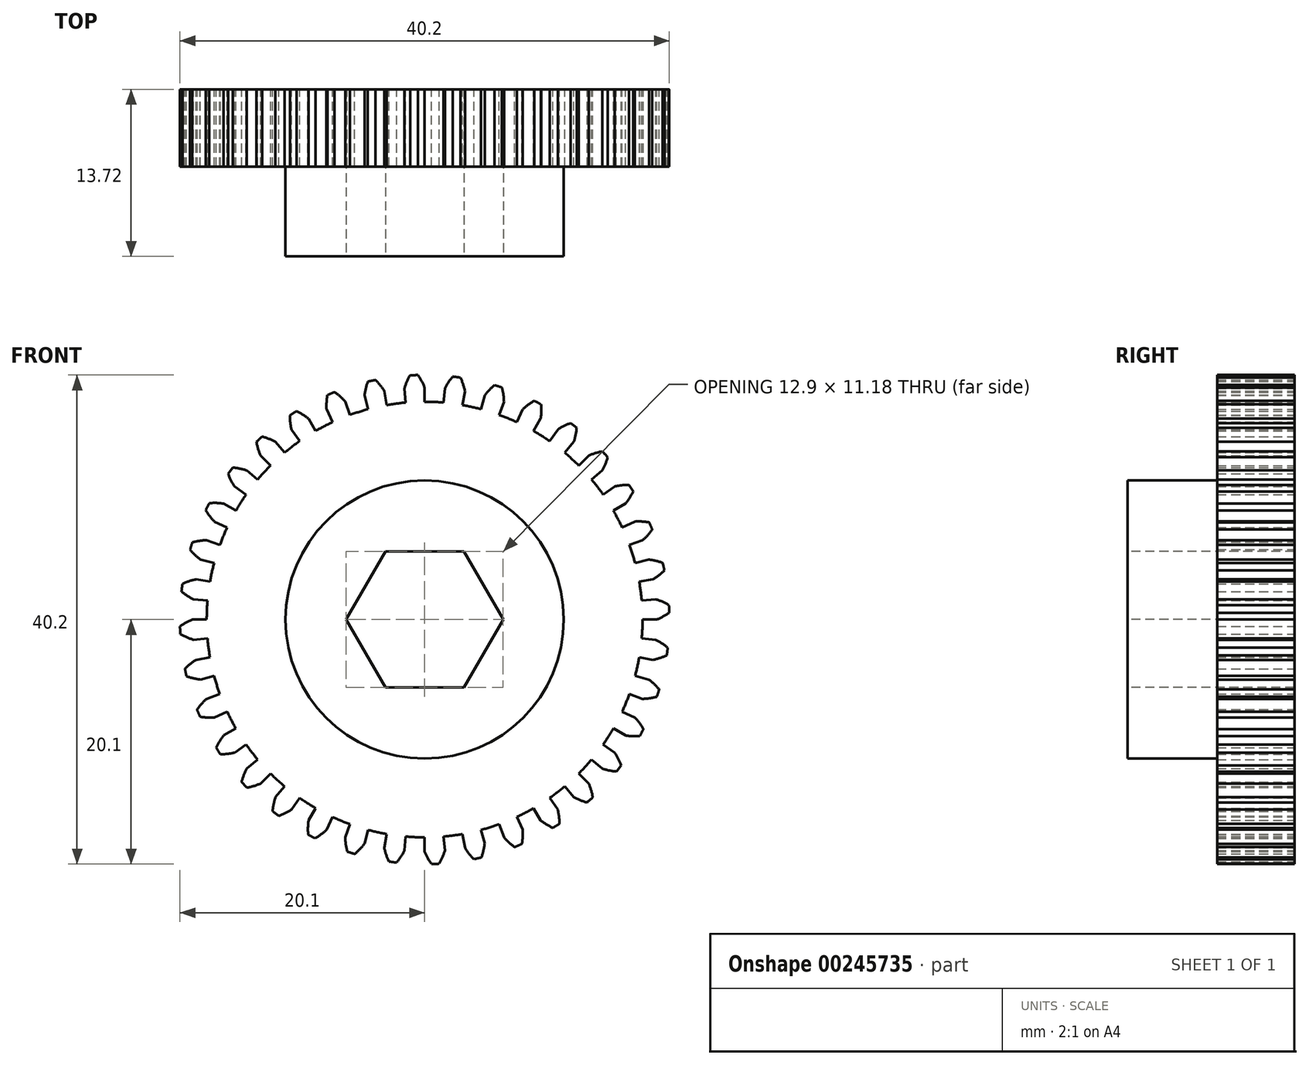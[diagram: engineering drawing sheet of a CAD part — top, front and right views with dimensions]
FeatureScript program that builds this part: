
annotation { "Feature Type Name" : "Feature", "Feature Type Description" : "" }
export const myFeature = defineFeature(function(context is Context, id is Id, definition is map)
    precondition{}
    {
        {
            var Q0;
            Q0=qCreatedBy(makeId("Front.planeOp"),FACE);
            var sketch = newSketch(context, id + "F0", { "sketchPlane" : qUnion([Q0])});
            skArc(sketch, "E0", {"start": v(0, 19.05) * mm, "mid": v(0, 19.05) * mm, "end": v(0, 19.05) * mm});
            skArc(sketch, "E1", {"start": v(-0.56, 20.1) * mm, "mid": v(-0.72, 20.1) * mm, "end": v(-0.88, 20.08) * mm});
            skLineSegment(sketch, "E2", {"start": v(0, 17.9) * mm, "end": v(0, 19.06) * mm});
            skLineSegment(sketch, "E3", {"start": v(0, 0) * mm, "end": v(-1.82, 41.68) * mm, "construction": true});
            skArc(sketch, "E4", {"start": v(1.56, 17.83) * mm, "mid": v(0.78, 17.88) * mm, "end": v(0, 17.9) * mm});
            skPoint(sketch, "E5", {"position": v(-4.44, 17.33) * mm});
            skArc(sketch, "E6.trimOffspring", {"start": v(0, 19.05) * mm, "mid": v(-0.25, 19.6) * mm, "end": v(-0.56, 20.1) * mm});
            skArc(sketch, "E7.MirrorCS", {"start": v(-1.66, 18.98) * mm, "mid": v(-1.46, 19.54) * mm, "end": v(-1.2, 20.07) * mm});
            skArc(sketch, "E8.MirrorCS", {"start": v(-1.2, 20.07) * mm, "mid": v(-1.04, 20.08) * mm, "end": v(-0.88, 20.08) * mm});
            skLineSegment(sketch, "E9.MirrorCS", {"start": v(-1.56, 17.83) * mm, "end": v(-1.66, 18.99) * mm});
            skPoint(sketch, "E10.orphan", {"position": v(-3.59, 41.01) * mm});
            skPoint(sketch, "E11.orphan", {"position": v(0, 41.17) * mm});
            skLineSegment(sketch, "E12.1.0", {"start": v(-4.63, 17.3) * mm, "end": v(-4.93, 18.4) * mm});
            skArc(sketch, "E12.1.1", {"start": v(-4.93, 18.4) * mm, "mid": v(-4.83, 18.99) * mm, "end": v(-4.66, 19.56) * mm});
            skArc(sketch, "E12.1.2", {"start": v(-4.66, 19.56) * mm, "mid": v(-4.5, 19.6) * mm, "end": v(-4.35, 19.63) * mm});
            skArc(sketch, "E12.1.3", {"start": v(-4.04, 19.7) * mm, "mid": v(-4.2, 19.66) * mm, "end": v(-4.35, 19.63) * mm});
            skArc(sketch, "E12.1.4", {"start": v(-3.3, 18.76) * mm, "mid": v(-3.64, 19.25) * mm, "end": v(-4.04, 19.7) * mm});
            skLineSegment(sketch, "E12.1.5", {"start": v(-3.1, 17.63) * mm, "end": v(-3.3, 18.77) * mm});
            skLineSegment(sketch, "E12.2.0", {"start": v(-7.57, 16.22) * mm, "end": v(-8.05, 17.27) * mm});
            skArc(sketch, "E12.2.1", {"start": v(-8.05, 17.26) * mm, "mid": v(-8.06, 17.86) * mm, "end": v(-7.99, 18.45) * mm});
            skArc(sketch, "E12.2.2", {"start": v(-7.99, 18.45) * mm, "mid": v(-7.84, 18.51) * mm, "end": v(-7.7, 18.57) * mm});
            skArc(sketch, "E12.2.3", {"start": v(-7.4, 18.7) * mm, "mid": v(-7.55, 18.63) * mm, "end": v(-7.7, 18.57) * mm});
            skArc(sketch, "E12.2.4", {"start": v(-6.51, 17.9) * mm, "mid": v(-6.93, 18.33) * mm, "end": v(-7.4, 18.7) * mm});
            skLineSegment(sketch, "E12.2.5", {"start": v(-6.12, 16.82) * mm, "end": v(-6.52, 17.9) * mm});
            skLineSegment(sketch, "E12.3.0", {"start": v(-10.27, 14.66) * mm, "end": v(-10.93, 15.61) * mm});
            skArc(sketch, "E12.3.1", {"start": v(-10.93, 15.6) * mm, "mid": v(-11.04, 16.19) * mm, "end": v(-11.07, 16.78) * mm});
            skArc(sketch, "E12.3.2", {"start": v(-11.07, 16.78) * mm, "mid": v(-10.94, 16.87) * mm, "end": v(-10.8, 16.96) * mm});
            skArc(sketch, "E12.3.3", {"start": v(-10.53, 17.12) * mm, "mid": v(-10.67, 17.04) * mm, "end": v(-10.8, 16.96) * mm});
            skArc(sketch, "E12.3.4", {"start": v(-9.52, 16.5) * mm, "mid": v(-10, 16.84) * mm, "end": v(-10.53, 17.12) * mm});
            skLineSegment(sketch, "E12.3.5", {"start": v(-8.95, 15.5) * mm, "end": v(-9.53, 16.5) * mm});
            skLineSegment(sketch, "E12.4.0", {"start": v(-12.66, 12.66) * mm, "end": v(-13.48, 13.48) * mm});
            skArc(sketch, "E12.4.1", {"start": v(-13.47, 13.47) * mm, "mid": v(-13.68, 14.03) * mm, "end": v(-13.81, 14.6) * mm});
            skArc(sketch, "E12.4.2", {"start": v(-13.81, 14.6) * mm, "mid": v(-13.7, 14.71) * mm, "end": v(-13.58, 14.82) * mm});
            skArc(sketch, "E12.4.3", {"start": v(-13.35, 15.04) * mm, "mid": v(-13.46, 14.93) * mm, "end": v(-13.58, 14.82) * mm});
            skArc(sketch, "E12.4.4", {"start": v(-12.24, 14.6) * mm, "mid": v(-12.78, 14.85) * mm, "end": v(-13.35, 15.04) * mm});
            skLineSegment(sketch, "E12.4.5", {"start": v(-11.5, 13.71) * mm, "end": v(-12.25, 14.6) * mm});
            skLineSegment(sketch, "E12.5.0", {"start": v(-14.66, 10.27) * mm, "end": v(-15.61, 10.93) * mm});
            skArc(sketch, "E12.5.1", {"start": v(-15.6, 10.92) * mm, "mid": v(-15.9, 11.44) * mm, "end": v(-16.14, 11.99) * mm});
            skArc(sketch, "E12.5.2", {"start": v(-16.14, 11.99) * mm, "mid": v(-16.05, 12.11) * mm, "end": v(-15.95, 12.24) * mm});
            skArc(sketch, "E12.5.3", {"start": v(-15.75, 12.49) * mm, "mid": v(-15.85, 12.36) * mm, "end": v(-15.95, 12.24) * mm});
            skArc(sketch, "E12.5.4", {"start": v(-14.6, 12.25) * mm, "mid": v(-15.17, 12.4) * mm, "end": v(-15.75, 12.49) * mm});
            skLineSegment(sketch, "E12.5.5", {"start": v(-13.71, 11.5) * mm, "end": v(-14.6, 12.25) * mm});
            skLineSegment(sketch, "E12.6.0", {"start": v(-16.22, 7.57) * mm, "end": v(-17.27, 8.05) * mm});
            skArc(sketch, "E12.6.1", {"start": v(-17.27, 8.05) * mm, "mid": v(-17.65, 8.5) * mm, "end": v(-17.98, 9) * mm});
            skArc(sketch, "E12.6.2", {"start": v(-17.98, 9) * mm, "mid": v(-17.9, 9.14) * mm, "end": v(-17.83, 9.28) * mm});
            skArc(sketch, "E12.6.3", {"start": v(-17.68, 9.56) * mm, "mid": v(-17.76, 9.42) * mm, "end": v(-17.83, 9.28) * mm});
            skArc(sketch, "E12.6.4", {"start": v(-16.5, 9.53) * mm, "mid": v(-17.09, 9.58) * mm, "end": v(-17.68, 9.56) * mm});
            skLineSegment(sketch, "E12.6.5", {"start": v(-15.5, 8.95) * mm, "end": v(-16.5, 9.53) * mm});
            skLineSegment(sketch, "E12.7.0", {"start": v(-17.3, 4.63) * mm, "end": v(-18.4, 4.93) * mm});
            skArc(sketch, "E12.7.1", {"start": v(-18.4, 4.93) * mm, "mid": v(-18.86, 5.3) * mm, "end": v(-19.27, 5.74) * mm});
            skArc(sketch, "E12.7.2", {"start": v(-19.27, 5.74) * mm, "mid": v(-19.22, 5.9) * mm, "end": v(-19.17, 6.05) * mm});
            skArc(sketch, "E12.7.3", {"start": v(-19.08, 6.35) * mm, "mid": v(-19.13, 6.2) * mm, "end": v(-19.17, 6.05) * mm});
            skArc(sketch, "E12.7.4", {"start": v(-17.9, 6.52) * mm, "mid": v(-18.5, 6.47) * mm, "end": v(-19.08, 6.35) * mm});
            skLineSegment(sketch, "E12.7.5", {"start": v(-16.82, 6.12) * mm, "end": v(-17.9, 6.52) * mm});
            skLineSegment(sketch, "E12.8.0", {"start": v(-17.83, 1.56) * mm, "end": v(-18.99, 1.66) * mm});
            skArc(sketch, "E12.8.1", {"start": v(-18.98, 1.66) * mm, "mid": v(-19.5, 1.95) * mm, "end": v(-19.97, 2.3) * mm});
            skArc(sketch, "E12.8.2", {"start": v(-19.97, 2.3) * mm, "mid": v(-19.95, 2.47) * mm, "end": v(-19.93, 2.62) * mm});
            skArc(sketch, "E12.8.3", {"start": v(-19.89, 2.94) * mm, "mid": v(-19.91, 2.78) * mm, "end": v(-19.93, 2.62) * mm});
            skArc(sketch, "E12.8.4", {"start": v(-18.76, 3.31) * mm, "mid": v(-19.34, 3.16) * mm, "end": v(-19.89, 2.94) * mm});
            skLineSegment(sketch, "E12.8.5", {"start": v(-17.63, 3.1) * mm, "end": v(-18.77, 3.3) * mm});
            skLineSegment(sketch, "E12.9.0", {"start": v(-17.83, -1.56) * mm, "end": v(-18.99, -1.66) * mm});
            skArc(sketch, "E12.9.1", {"start": v(-18.98, -1.66) * mm, "mid": v(-19.54, -1.46) * mm, "end": v(-20.07, -1.2) * mm});
            skArc(sketch, "E12.9.2", {"start": v(-20.07, -1.2) * mm, "mid": v(-20.08, -1.04) * mm, "end": v(-20.08, -0.88) * mm});
            skArc(sketch, "E12.9.3", {"start": v(-20.1, -0.56) * mm, "mid": v(-20.1, -0.72) * mm, "end": v(-20.08, -0.88) * mm});
            skArc(sketch, "E12.9.4", {"start": v(-19.05, 0) * mm, "mid": v(-19.6, -0.25) * mm, "end": v(-20.1, -0.56) * mm});
            skLineSegment(sketch, "E12.9.5", {"start": v(-17.9, 0) * mm, "end": v(-19.06, 0) * mm});
            skLineSegment(sketch, "E12.10.0", {"start": v(-17.3, -4.63) * mm, "end": v(-18.4, -4.93) * mm});
            skArc(sketch, "E12.10.1", {"start": v(-18.4, -4.93) * mm, "mid": v(-18.99, -4.83) * mm, "end": v(-19.56, -4.66) * mm});
            skArc(sketch, "E12.10.2", {"start": v(-19.56, -4.66) * mm, "mid": v(-19.6, -4.5) * mm, "end": v(-19.63, -4.35) * mm});
            skArc(sketch, "E12.10.3", {"start": v(-19.7, -4.04) * mm, "mid": v(-19.66, -4.2) * mm, "end": v(-19.63, -4.35) * mm});
            skArc(sketch, "E12.10.4", {"start": v(-18.76, -3.3) * mm, "mid": v(-19.25, -3.64) * mm, "end": v(-19.7, -4.04) * mm});
            skLineSegment(sketch, "E12.10.5", {"start": v(-17.63, -3.1) * mm, "end": v(-18.77, -3.3) * mm});
            skLineSegment(sketch, "E12.11.0", {"start": v(-16.22, -7.57) * mm, "end": v(-17.27, -8.05) * mm});
            skArc(sketch, "E12.11.1", {"start": v(-17.26, -8.05) * mm, "mid": v(-17.86, -8.06) * mm, "end": v(-18.45, -7.99) * mm});
            skArc(sketch, "E12.11.2", {"start": v(-18.45, -7.99) * mm, "mid": v(-18.51, -7.84) * mm, "end": v(-18.57, -7.7) * mm});
            skArc(sketch, "E12.11.3", {"start": v(-18.7, -7.4) * mm, "mid": v(-18.63, -7.55) * mm, "end": v(-18.57, -7.7) * mm});
            skArc(sketch, "E12.11.4", {"start": v(-17.9, -6.51) * mm, "mid": v(-18.33, -6.93) * mm, "end": v(-18.7, -7.4) * mm});
            skLineSegment(sketch, "E12.11.5", {"start": v(-16.82, -6.12) * mm, "end": v(-17.9, -6.52) * mm});
            skLineSegment(sketch, "E12.12.0", {"start": v(-14.66, -10.27) * mm, "end": v(-15.61, -10.93) * mm});
            skArc(sketch, "E12.12.1", {"start": v(-15.6, -10.93) * mm, "mid": v(-16.19, -11.04) * mm, "end": v(-16.78, -11.07) * mm});
            skArc(sketch, "E12.12.2", {"start": v(-16.78, -11.07) * mm, "mid": v(-16.87, -10.94) * mm, "end": v(-16.96, -10.8) * mm});
            skArc(sketch, "E12.12.3", {"start": v(-17.12, -10.53) * mm, "mid": v(-17.04, -10.67) * mm, "end": v(-16.96, -10.8) * mm});
            skArc(sketch, "E12.12.4", {"start": v(-16.5, -9.52) * mm, "mid": v(-16.84, -10) * mm, "end": v(-17.12, -10.53) * mm});
            skLineSegment(sketch, "E12.12.5", {"start": v(-15.5, -8.95) * mm, "end": v(-16.5, -9.53) * mm});
            skLineSegment(sketch, "E12.13.0", {"start": v(-12.66, -12.66) * mm, "end": v(-13.48, -13.48) * mm});
            skArc(sketch, "E12.13.1", {"start": v(-13.47, -13.47) * mm, "mid": v(-14.03, -13.68) * mm, "end": v(-14.6, -13.81) * mm});
            skArc(sketch, "E12.13.2", {"start": v(-14.6, -13.81) * mm, "mid": v(-14.71, -13.7) * mm, "end": v(-14.82, -13.58) * mm});
            skArc(sketch, "E12.13.3", {"start": v(-15.04, -13.35) * mm, "mid": v(-14.93, -13.46) * mm, "end": v(-14.82, -13.58) * mm});
            skArc(sketch, "E12.13.4", {"start": v(-14.6, -12.24) * mm, "mid": v(-14.85, -12.78) * mm, "end": v(-15.04, -13.35) * mm});
            skLineSegment(sketch, "E12.13.5", {"start": v(-13.71, -11.5) * mm, "end": v(-14.6, -12.25) * mm});
            skLineSegment(sketch, "E12.14.0", {"start": v(-10.27, -14.66) * mm, "end": v(-10.93, -15.61) * mm});
            skArc(sketch, "E12.14.1", {"start": v(-10.92, -15.6) * mm, "mid": v(-11.44, -15.9) * mm, "end": v(-11.99, -16.14) * mm});
            skArc(sketch, "E12.14.2", {"start": v(-11.99, -16.14) * mm, "mid": v(-12.11, -16.05) * mm, "end": v(-12.24, -15.95) * mm});
            skArc(sketch, "E12.14.3", {"start": v(-12.49, -15.75) * mm, "mid": v(-12.36, -15.85) * mm, "end": v(-12.24, -15.95) * mm});
            skArc(sketch, "E12.14.4", {"start": v(-12.25, -14.6) * mm, "mid": v(-12.4, -15.17) * mm, "end": v(-12.49, -15.75) * mm});
            skLineSegment(sketch, "E12.14.5", {"start": v(-11.5, -13.71) * mm, "end": v(-12.25, -14.6) * mm});
            skLineSegment(sketch, "E12.15.0", {"start": v(-7.57, -16.22) * mm, "end": v(-8.05, -17.27) * mm});
            skArc(sketch, "E12.15.1", {"start": v(-8.05, -17.27) * mm, "mid": v(-8.5, -17.65) * mm, "end": v(-9, -17.98) * mm});
            skArc(sketch, "E12.15.2", {"start": v(-9, -17.98) * mm, "mid": v(-9.14, -17.9) * mm, "end": v(-9.28, -17.83) * mm});
            skArc(sketch, "E12.15.3", {"start": v(-9.56, -17.68) * mm, "mid": v(-9.42, -17.76) * mm, "end": v(-9.28, -17.83) * mm});
            skArc(sketch, "E12.15.4", {"start": v(-9.53, -16.5) * mm, "mid": v(-9.58, -17.09) * mm, "end": v(-9.56, -17.68) * mm});
            skLineSegment(sketch, "E12.15.5", {"start": v(-8.95, -15.5) * mm, "end": v(-9.53, -16.5) * mm});
            skLineSegment(sketch, "E12.16.0", {"start": v(-4.63, -17.3) * mm, "end": v(-4.93, -18.4) * mm});
            skArc(sketch, "E12.16.1", {"start": v(-4.93, -18.4) * mm, "mid": v(-5.3, -18.86) * mm, "end": v(-5.74, -19.27) * mm});
            skArc(sketch, "E12.16.2", {"start": v(-5.74, -19.27) * mm, "mid": v(-5.9, -19.22) * mm, "end": v(-6.05, -19.17) * mm});
            skArc(sketch, "E12.16.3", {"start": v(-6.35, -19.08) * mm, "mid": v(-6.2, -19.13) * mm, "end": v(-6.05, -19.17) * mm});
            skArc(sketch, "E12.16.4", {"start": v(-6.52, -17.9) * mm, "mid": v(-6.47, -18.5) * mm, "end": v(-6.35, -19.08) * mm});
            skLineSegment(sketch, "E12.16.5", {"start": v(-6.12, -16.82) * mm, "end": v(-6.52, -17.9) * mm});
            skLineSegment(sketch, "E12.17.0", {"start": v(-1.56, -17.83) * mm, "end": v(-1.66, -18.99) * mm});
            skArc(sketch, "E12.17.1", {"start": v(-1.66, -18.98) * mm, "mid": v(-1.95, -19.5) * mm, "end": v(-2.3, -19.97) * mm});
            skArc(sketch, "E12.17.2", {"start": v(-2.3, -19.97) * mm, "mid": v(-2.47, -19.95) * mm, "end": v(-2.62, -19.93) * mm});
            skArc(sketch, "E12.17.3", {"start": v(-2.94, -19.89) * mm, "mid": v(-2.78, -19.91) * mm, "end": v(-2.62, -19.93) * mm});
            skArc(sketch, "E12.17.4", {"start": v(-3.31, -18.76) * mm, "mid": v(-3.16, -19.34) * mm, "end": v(-2.94, -19.89) * mm});
            skLineSegment(sketch, "E12.17.5", {"start": v(-3.1, -17.63) * mm, "end": v(-3.3, -18.77) * mm});
            skLineSegment(sketch, "E12.18.0", {"start": v(1.56, -17.83) * mm, "end": v(1.66, -18.99) * mm});
            skArc(sketch, "E12.18.1", {"start": v(1.66, -18.98) * mm, "mid": v(1.46, -19.54) * mm, "end": v(1.2, -20.07) * mm});
            skArc(sketch, "E12.18.2", {"start": v(1.2, -20.07) * mm, "mid": v(1.04, -20.08) * mm, "end": v(0.88, -20.08) * mm});
            skArc(sketch, "E12.18.3", {"start": v(0.56, -20.1) * mm, "mid": v(0.72, -20.1) * mm, "end": v(0.88, -20.08) * mm});
            skArc(sketch, "E12.18.4", {"start": v(0, -19.05) * mm, "mid": v(0.25, -19.6) * mm, "end": v(0.56, -20.1) * mm});
            skLineSegment(sketch, "E12.18.5", {"start": v(0, -17.9) * mm, "end": v(0, -19.06) * mm});
            skLineSegment(sketch, "E12.19.0", {"start": v(4.63, -17.3) * mm, "end": v(4.93, -18.4) * mm});
            skArc(sketch, "E12.19.1", {"start": v(4.93, -18.4) * mm, "mid": v(4.83, -18.99) * mm, "end": v(4.66, -19.56) * mm});
            skArc(sketch, "E12.19.2", {"start": v(4.66, -19.56) * mm, "mid": v(4.5, -19.6) * mm, "end": v(4.35, -19.63) * mm});
            skArc(sketch, "E12.19.3", {"start": v(4.04, -19.7) * mm, "mid": v(4.2, -19.66) * mm, "end": v(4.35, -19.63) * mm});
            skArc(sketch, "E12.19.4", {"start": v(3.3, -18.76) * mm, "mid": v(3.64, -19.25) * mm, "end": v(4.04, -19.7) * mm});
            skLineSegment(sketch, "E12.19.5", {"start": v(3.1, -17.63) * mm, "end": v(3.3, -18.77) * mm});
            skLineSegment(sketch, "E12.20.0", {"start": v(7.57, -16.22) * mm, "end": v(8.05, -17.27) * mm});
            skArc(sketch, "E12.20.1", {"start": v(8.05, -17.26) * mm, "mid": v(8.06, -17.86) * mm, "end": v(7.99, -18.45) * mm});
            skArc(sketch, "E12.20.2", {"start": v(7.99, -18.45) * mm, "mid": v(7.84, -18.51) * mm, "end": v(7.7, -18.57) * mm});
            skArc(sketch, "E12.20.3", {"start": v(7.4, -18.7) * mm, "mid": v(7.55, -18.63) * mm, "end": v(7.7, -18.57) * mm});
            skArc(sketch, "E12.20.4", {"start": v(6.51, -17.9) * mm, "mid": v(6.93, -18.33) * mm, "end": v(7.4, -18.7) * mm});
            skLineSegment(sketch, "E12.20.5", {"start": v(6.12, -16.82) * mm, "end": v(6.52, -17.9) * mm});
            skLineSegment(sketch, "E12.21.0", {"start": v(10.27, -14.66) * mm, "end": v(10.93, -15.61) * mm});
            skArc(sketch, "E12.21.1", {"start": v(10.93, -15.6) * mm, "mid": v(11.04, -16.19) * mm, "end": v(11.07, -16.78) * mm});
            skArc(sketch, "E12.21.2", {"start": v(11.07, -16.78) * mm, "mid": v(10.94, -16.87) * mm, "end": v(10.8, -16.96) * mm});
            skArc(sketch, "E12.21.3", {"start": v(10.53, -17.12) * mm, "mid": v(10.67, -17.04) * mm, "end": v(10.8, -16.96) * mm});
            skArc(sketch, "E12.21.4", {"start": v(9.52, -16.5) * mm, "mid": v(10, -16.84) * mm, "end": v(10.53, -17.12) * mm});
            skLineSegment(sketch, "E12.21.5", {"start": v(8.95, -15.5) * mm, "end": v(9.53, -16.5) * mm});
            skLineSegment(sketch, "E12.22.0", {"start": v(12.66, -12.66) * mm, "end": v(13.48, -13.48) * mm});
            skArc(sketch, "E12.22.1", {"start": v(13.47, -13.47) * mm, "mid": v(13.68, -14.03) * mm, "end": v(13.81, -14.6) * mm});
            skArc(sketch, "E12.22.2", {"start": v(13.81, -14.6) * mm, "mid": v(13.7, -14.71) * mm, "end": v(13.58, -14.82) * mm});
            skArc(sketch, "E12.22.3", {"start": v(13.35, -15.04) * mm, "mid": v(13.46, -14.93) * mm, "end": v(13.58, -14.82) * mm});
            skArc(sketch, "E12.22.4", {"start": v(12.24, -14.6) * mm, "mid": v(12.78, -14.85) * mm, "end": v(13.35, -15.04) * mm});
            skLineSegment(sketch, "E12.22.5", {"start": v(11.5, -13.71) * mm, "end": v(12.25, -14.6) * mm});
            skLineSegment(sketch, "E12.23.0", {"start": v(14.66, -10.27) * mm, "end": v(15.61, -10.93) * mm});
            skArc(sketch, "E12.23.1", {"start": v(15.6, -10.92) * mm, "mid": v(15.9, -11.44) * mm, "end": v(16.14, -11.99) * mm});
            skArc(sketch, "E12.23.2", {"start": v(16.14, -11.99) * mm, "mid": v(16.05, -12.11) * mm, "end": v(15.95, -12.24) * mm});
            skArc(sketch, "E12.23.3", {"start": v(15.75, -12.49) * mm, "mid": v(15.85, -12.36) * mm, "end": v(15.95, -12.24) * mm});
            skArc(sketch, "E12.23.4", {"start": v(14.6, -12.25) * mm, "mid": v(15.17, -12.4) * mm, "end": v(15.75, -12.49) * mm});
            skLineSegment(sketch, "E12.23.5", {"start": v(13.71, -11.5) * mm, "end": v(14.6, -12.25) * mm});
            skLineSegment(sketch, "E12.24.0", {"start": v(16.22, -7.57) * mm, "end": v(17.27, -8.05) * mm});
            skArc(sketch, "E12.24.1", {"start": v(17.27, -8.05) * mm, "mid": v(17.65, -8.5) * mm, "end": v(17.98, -9) * mm});
            skArc(sketch, "E12.24.2", {"start": v(17.98, -9) * mm, "mid": v(17.9, -9.14) * mm, "end": v(17.83, -9.28) * mm});
            skArc(sketch, "E12.24.3", {"start": v(17.68, -9.56) * mm, "mid": v(17.76, -9.42) * mm, "end": v(17.83, -9.28) * mm});
            skArc(sketch, "E12.24.4", {"start": v(16.5, -9.53) * mm, "mid": v(17.09, -9.58) * mm, "end": v(17.68, -9.56) * mm});
            skLineSegment(sketch, "E12.24.5", {"start": v(15.5, -8.95) * mm, "end": v(16.5, -9.53) * mm});
            skLineSegment(sketch, "E12.25.0", {"start": v(17.3, -4.63) * mm, "end": v(18.4, -4.93) * mm});
            skArc(sketch, "E12.25.1", {"start": v(18.4, -4.93) * mm, "mid": v(18.86, -5.3) * mm, "end": v(19.27, -5.74) * mm});
            skArc(sketch, "E12.25.2", {"start": v(19.27, -5.74) * mm, "mid": v(19.22, -5.9) * mm, "end": v(19.17, -6.05) * mm});
            skArc(sketch, "E12.25.3", {"start": v(19.08, -6.35) * mm, "mid": v(19.13, -6.2) * mm, "end": v(19.17, -6.05) * mm});
            skArc(sketch, "E12.25.4", {"start": v(17.9, -6.52) * mm, "mid": v(18.5, -6.47) * mm, "end": v(19.08, -6.35) * mm});
            skLineSegment(sketch, "E12.25.5", {"start": v(16.82, -6.12) * mm, "end": v(17.9, -6.52) * mm});
            skLineSegment(sketch, "E12.26.0", {"start": v(17.83, -1.56) * mm, "end": v(18.99, -1.66) * mm});
            skArc(sketch, "E12.26.1", {"start": v(18.98, -1.66) * mm, "mid": v(19.5, -1.95) * mm, "end": v(19.97, -2.3) * mm});
            skArc(sketch, "E12.26.2", {"start": v(19.97, -2.3) * mm, "mid": v(19.95, -2.47) * mm, "end": v(19.93, -2.62) * mm});
            skArc(sketch, "E12.26.3", {"start": v(19.89, -2.94) * mm, "mid": v(19.91, -2.78) * mm, "end": v(19.93, -2.62) * mm});
            skArc(sketch, "E12.26.4", {"start": v(18.76, -3.31) * mm, "mid": v(19.34, -3.16) * mm, "end": v(19.89, -2.94) * mm});
            skLineSegment(sketch, "E12.26.5", {"start": v(17.63, -3.1) * mm, "end": v(18.77, -3.3) * mm});
            skLineSegment(sketch, "E12.27.0", {"start": v(17.83, 1.56) * mm, "end": v(18.99, 1.66) * mm});
            skArc(sketch, "E12.27.1", {"start": v(18.98, 1.66) * mm, "mid": v(19.54, 1.46) * mm, "end": v(20.07, 1.2) * mm});
            skArc(sketch, "E12.27.2", {"start": v(20.07, 1.2) * mm, "mid": v(20.08, 1.04) * mm, "end": v(20.08, 0.88) * mm});
            skArc(sketch, "E12.27.3", {"start": v(20.1, 0.56) * mm, "mid": v(20.1, 0.72) * mm, "end": v(20.08, 0.88) * mm});
            skArc(sketch, "E12.27.4", {"start": v(19.05, 0) * mm, "mid": v(19.6, 0.25) * mm, "end": v(20.1, 0.56) * mm});
            skLineSegment(sketch, "E12.27.5", {"start": v(17.9, 0) * mm, "end": v(19.06, 0) * mm});
            skLineSegment(sketch, "E12.28.0", {"start": v(17.3, 4.63) * mm, "end": v(18.4, 4.93) * mm});
            skArc(sketch, "E12.28.1", {"start": v(18.4, 4.93) * mm, "mid": v(18.99, 4.83) * mm, "end": v(19.56, 4.66) * mm});
            skArc(sketch, "E12.28.2", {"start": v(19.56, 4.66) * mm, "mid": v(19.6, 4.5) * mm, "end": v(19.63, 4.35) * mm});
            skArc(sketch, "E12.28.3", {"start": v(19.7, 4.04) * mm, "mid": v(19.66, 4.2) * mm, "end": v(19.63, 4.35) * mm});
            skArc(sketch, "E12.28.4", {"start": v(18.76, 3.3) * mm, "mid": v(19.25, 3.64) * mm, "end": v(19.7, 4.04) * mm});
            skLineSegment(sketch, "E12.28.5", {"start": v(17.63, 3.1) * mm, "end": v(18.77, 3.3) * mm});
            skLineSegment(sketch, "E12.29.0", {"start": v(16.22, 7.57) * mm, "end": v(17.27, 8.05) * mm});
            skArc(sketch, "E12.29.1", {"start": v(17.26, 8.05) * mm, "mid": v(17.86, 8.06) * mm, "end": v(18.45, 7.99) * mm});
            skArc(sketch, "E12.29.2", {"start": v(18.45, 7.99) * mm, "mid": v(18.51, 7.84) * mm, "end": v(18.57, 7.7) * mm});
            skArc(sketch, "E12.29.3", {"start": v(18.7, 7.4) * mm, "mid": v(18.63, 7.55) * mm, "end": v(18.57, 7.7) * mm});
            skArc(sketch, "E12.29.4", {"start": v(17.9, 6.51) * mm, "mid": v(18.33, 6.93) * mm, "end": v(18.7, 7.4) * mm});
            skLineSegment(sketch, "E12.29.5", {"start": v(16.82, 6.12) * mm, "end": v(17.9, 6.52) * mm});
            skLineSegment(sketch, "E12.30.0", {"start": v(14.66, 10.27) * mm, "end": v(15.61, 10.93) * mm});
            skArc(sketch, "E12.30.1", {"start": v(15.6, 10.93) * mm, "mid": v(16.19, 11.04) * mm, "end": v(16.78, 11.07) * mm});
            skArc(sketch, "E12.30.2", {"start": v(16.78, 11.07) * mm, "mid": v(16.87, 10.94) * mm, "end": v(16.96, 10.8) * mm});
            skArc(sketch, "E12.30.3", {"start": v(17.12, 10.53) * mm, "mid": v(17.04, 10.67) * mm, "end": v(16.96, 10.8) * mm});
            skArc(sketch, "E12.30.4", {"start": v(16.5, 9.52) * mm, "mid": v(16.84, 10) * mm, "end": v(17.12, 10.53) * mm});
            skLineSegment(sketch, "E12.30.5", {"start": v(15.5, 8.95) * mm, "end": v(16.5, 9.53) * mm});
            skLineSegment(sketch, "E12.31.0", {"start": v(12.66, 12.66) * mm, "end": v(13.48, 13.48) * mm});
            skArc(sketch, "E12.31.1", {"start": v(13.47, 13.47) * mm, "mid": v(14.03, 13.68) * mm, "end": v(14.6, 13.81) * mm});
            skArc(sketch, "E12.31.2", {"start": v(14.6, 13.81) * mm, "mid": v(14.71, 13.7) * mm, "end": v(14.82, 13.58) * mm});
            skArc(sketch, "E12.31.3", {"start": v(15.04, 13.35) * mm, "mid": v(14.93, 13.46) * mm, "end": v(14.82, 13.58) * mm});
            skArc(sketch, "E12.31.4", {"start": v(14.6, 12.24) * mm, "mid": v(14.85, 12.78) * mm, "end": v(15.04, 13.35) * mm});
            skLineSegment(sketch, "E12.31.5", {"start": v(13.71, 11.5) * mm, "end": v(14.6, 12.25) * mm});
            skLineSegment(sketch, "E12.32.0", {"start": v(10.27, 14.66) * mm, "end": v(10.93, 15.61) * mm});
            skArc(sketch, "E12.32.1", {"start": v(10.92, 15.6) * mm, "mid": v(11.44, 15.9) * mm, "end": v(11.99, 16.14) * mm});
            skArc(sketch, "E12.32.2", {"start": v(11.99, 16.14) * mm, "mid": v(12.11, 16.05) * mm, "end": v(12.24, 15.95) * mm});
            skArc(sketch, "E12.32.3", {"start": v(12.49, 15.75) * mm, "mid": v(12.36, 15.85) * mm, "end": v(12.24, 15.95) * mm});
            skArc(sketch, "E12.32.4", {"start": v(12.25, 14.6) * mm, "mid": v(12.4, 15.17) * mm, "end": v(12.49, 15.75) * mm});
            skLineSegment(sketch, "E12.32.5", {"start": v(11.5, 13.71) * mm, "end": v(12.25, 14.6) * mm});
            skLineSegment(sketch, "E12.33.0", {"start": v(7.57, 16.22) * mm, "end": v(8.05, 17.27) * mm});
            skArc(sketch, "E12.33.1", {"start": v(8.05, 17.27) * mm, "mid": v(8.5, 17.65) * mm, "end": v(9, 17.98) * mm});
            skArc(sketch, "E12.33.2", {"start": v(9, 17.98) * mm, "mid": v(9.14, 17.9) * mm, "end": v(9.28, 17.83) * mm});
            skArc(sketch, "E12.33.3", {"start": v(9.56, 17.68) * mm, "mid": v(9.42, 17.76) * mm, "end": v(9.28, 17.83) * mm});
            skArc(sketch, "E12.33.4", {"start": v(9.53, 16.5) * mm, "mid": v(9.58, 17.09) * mm, "end": v(9.56, 17.68) * mm});
            skLineSegment(sketch, "E12.33.5", {"start": v(8.95, 15.5) * mm, "end": v(9.53, 16.5) * mm});
            skLineSegment(sketch, "E12.34.0", {"start": v(4.63, 17.3) * mm, "end": v(4.93, 18.4) * mm});
            skArc(sketch, "E12.34.1", {"start": v(4.93, 18.4) * mm, "mid": v(5.3, 18.86) * mm, "end": v(5.74, 19.27) * mm});
            skArc(sketch, "E12.34.2", {"start": v(5.74, 19.27) * mm, "mid": v(5.9, 19.22) * mm, "end": v(6.05, 19.17) * mm});
            skArc(sketch, "E12.34.3", {"start": v(6.35, 19.08) * mm, "mid": v(6.2, 19.13) * mm, "end": v(6.05, 19.17) * mm});
            skArc(sketch, "E12.34.4", {"start": v(6.52, 17.9) * mm, "mid": v(6.47, 18.5) * mm, "end": v(6.35, 19.08) * mm});
            skLineSegment(sketch, "E12.34.5", {"start": v(6.12, 16.82) * mm, "end": v(6.52, 17.9) * mm});
            skLineSegment(sketch, "E12.35.0", {"start": v(1.56, 17.83) * mm, "end": v(1.66, 18.99) * mm});
            skArc(sketch, "E12.35.1", {"start": v(1.66, 18.98) * mm, "mid": v(1.95, 19.5) * mm, "end": v(2.3, 19.97) * mm});
            skArc(sketch, "E12.35.2", {"start": v(2.3, 19.97) * mm, "mid": v(2.47, 19.95) * mm, "end": v(2.62, 19.93) * mm});
            skArc(sketch, "E12.35.3", {"start": v(2.94, 19.89) * mm, "mid": v(2.78, 19.91) * mm, "end": v(2.62, 19.93) * mm});
            skArc(sketch, "E12.35.4", {"start": v(3.31, 18.76) * mm, "mid": v(3.16, 19.34) * mm, "end": v(2.94, 19.89) * mm});
            skLineSegment(sketch, "E12.35.5", {"start": v(3.1, 17.63) * mm, "end": v(3.3, 18.77) * mm});
            skArc(sketch, "E13.trimOffspring", {"start": v(4.63, 17.3) * mm, "mid": v(3.87, 17.48) * mm, "end": v(3.1, 17.63) * mm});
            skArc(sketch, "E14.trimOffspring", {"start": v(7.57, 16.22) * mm, "mid": v(6.85, 16.54) * mm, "end": v(6.12, 16.82) * mm});
            skArc(sketch, "E15.trimOffspring", {"start": v(10.27, 14.66) * mm, "mid": v(9.62, 15.1) * mm, "end": v(8.95, 15.5) * mm});
            skArc(sketch, "E16.trimOffspring", {"start": v(12.66, 12.66) * mm, "mid": v(12.1, 13.2) * mm, "end": v(11.5, 13.71) * mm});
            skArc(sketch, "E17.trimOffspring", {"start": v(14.66, 10.27) * mm, "mid": v(14.2, 10.9) * mm, "end": v(13.71, 11.5) * mm});
            skArc(sketch, "E18.trimOffspring", {"start": v(16.22, 7.57) * mm, "mid": v(15.88, 8.27) * mm, "end": v(15.5, 8.95) * mm});
            skArc(sketch, "E19.trimOffspring", {"start": v(17.3, 4.63) * mm, "mid": v(17.07, 5.38) * mm, "end": v(16.82, 6.12) * mm});
            skArc(sketch, "E20.trimOffspring", {"start": v(17.83, 1.56) * mm, "mid": v(17.75, 2.34) * mm, "end": v(17.63, 3.1) * mm});
            skArc(sketch, "E21.trimOffspring", {"start": v(17.83, -1.56) * mm, "mid": v(17.88, -0.78) * mm, "end": v(17.9, 0) * mm});
            skArc(sketch, "E22.trimOffspring", {"start": v(17.3, -4.63) * mm, "mid": v(17.48, -3.87) * mm, "end": v(17.63, -3.1) * mm});
            skArc(sketch, "E23.trimOffspring", {"start": v(16.22, -7.57) * mm, "mid": v(16.54, -6.85) * mm, "end": v(16.82, -6.12) * mm});
            skArc(sketch, "E24.trimOffspring", {"start": v(14.66, -10.27) * mm, "mid": v(15.1, -9.62) * mm, "end": v(15.5, -8.95) * mm});
            skArc(sketch, "E25.trimOffspring", {"start": v(12.66, -12.66) * mm, "mid": v(13.2, -12.1) * mm, "end": v(13.71, -11.5) * mm});
            skArc(sketch, "E26.trimOffspring", {"start": v(10.27, -14.66) * mm, "mid": v(10.9, -14.2) * mm, "end": v(11.5, -13.71) * mm});
            skArc(sketch, "E27.trimOffspring", {"start": v(7.57, -16.22) * mm, "mid": v(8.27, -15.88) * mm, "end": v(8.95, -15.5) * mm});
            skArc(sketch, "E28.trimOffspring", {"start": v(4.63, -17.3) * mm, "mid": v(5.38, -17.07) * mm, "end": v(6.12, -16.82) * mm});
            skArc(sketch, "E29.trimOffspring", {"start": v(1.56, -17.83) * mm, "mid": v(2.34, -17.75) * mm, "end": v(3.1, -17.63) * mm});
            skArc(sketch, "E30.trimOffspring", {"start": v(-1.56, -17.83) * mm, "mid": v(-0.78, -17.88) * mm, "end": v(0, -17.9) * mm});
            skArc(sketch, "E31.trimOffspring", {"start": v(-4.63, -17.3) * mm, "mid": v(-3.87, -17.48) * mm, "end": v(-3.1, -17.63) * mm});
            skArc(sketch, "E32.trimOffspring", {"start": v(-7.57, -16.22) * mm, "mid": v(-6.85, -16.54) * mm, "end": v(-6.12, -16.82) * mm});
            skArc(sketch, "E33.trimOffspring", {"start": v(-10.27, -14.66) * mm, "mid": v(-9.62, -15.1) * mm, "end": v(-8.95, -15.5) * mm});
            skArc(sketch, "E34.trimOffspring", {"start": v(-12.66, -12.66) * mm, "mid": v(-12.1, -13.2) * mm, "end": v(-11.5, -13.71) * mm});
            skArc(sketch, "E35.trimOffspring", {"start": v(-14.66, -10.27) * mm, "mid": v(-14.2, -10.9) * mm, "end": v(-13.71, -11.5) * mm});
            skArc(sketch, "E36.trimOffspring", {"start": v(-16.22, -7.57) * mm, "mid": v(-15.88, -8.27) * mm, "end": v(-15.5, -8.95) * mm});
            skArc(sketch, "E37.trimOffspring", {"start": v(-17.3, -4.63) * mm, "mid": v(-17.07, -5.38) * mm, "end": v(-16.82, -6.12) * mm});
            skArc(sketch, "E38.trimOffspring", {"start": v(-17.83, -1.56) * mm, "mid": v(-17.75, -2.34) * mm, "end": v(-17.63, -3.1) * mm});
            skArc(sketch, "E39.trimOffspring", {"start": v(-17.83, 1.56) * mm, "mid": v(-17.88, 0.78) * mm, "end": v(-17.9, 0) * mm});
            skArc(sketch, "E40.trimOffspring", {"start": v(-17.3, 4.63) * mm, "mid": v(-17.48, 3.87) * mm, "end": v(-17.63, 3.1) * mm});
            skArc(sketch, "E41.trimOffspring", {"start": v(-16.22, 7.57) * mm, "mid": v(-16.54, 6.85) * mm, "end": v(-16.82, 6.12) * mm});
            skArc(sketch, "E42.trimOffspring", {"start": v(-14.66, 10.27) * mm, "mid": v(-15.1, 9.62) * mm, "end": v(-15.5, 8.95) * mm});
            skArc(sketch, "E43.trimOffspring", {"start": v(-12.66, 12.66) * mm, "mid": v(-13.2, 12.1) * mm, "end": v(-13.71, 11.5) * mm});
            skArc(sketch, "E44.trimOffspring", {"start": v(-10.27, 14.66) * mm, "mid": v(-10.9, 14.2) * mm, "end": v(-11.5, 13.71) * mm});
            skArc(sketch, "E45.trimOffspring", {"start": v(-7.57, 16.22) * mm, "mid": v(-8.27, 15.88) * mm, "end": v(-8.95, 15.5) * mm});
            skArc(sketch, "E46.trimOffspring", {"start": v(-4.63, 17.3) * mm, "mid": v(-5.38, 17.07) * mm, "end": v(-6.12, 16.82) * mm});
            skArc(sketch, "E47.trimOffspring", {"start": v(-1.56, 17.83) * mm, "mid": v(-2.34, 17.75) * mm, "end": v(-3.1, 17.63) * mm});
            skSolve(sketch);
        }
        {
            var Q0;
            Q0 = qSketchRegion(id + "F0", true);
            extrude(context, id + "F1", {"entities" : qUnion([Q0]), "depth" : 6.35 * mm});
        }
        {
            var Q0;
            Q0=makeQuery(id+"F1.opExtrude","CAP_FACE",FACE,{"disambiguationData":[OSD([sQuery(id+"F0.wireOp",EDGE,"E0"),sQuery(id+"F0.wireOp",EDGE,"E1"),sQuery(id+"F0.wireOp",EDGE,"E2"),sQuery(id+"F0.wireOp",EDGE,"E4"),sQuery(id+"F0.wireOp",EDGE,"E6.trimOffspring"),sQuery(id+"F0.wireOp",EDGE,"E7.MirrorCS"),sQuery(id+"F0.wireOp",EDGE,"E8.MirrorCS"),sQuery(id+"F0.wireOp",EDGE,"E9.MirrorCS"),sQuery(id+"F0.wireOp",EDGE,"E12.1.0"),sQuery(id+"F0.wireOp",EDGE,"E12.1.1"),sQuery(id+"F0.wireOp",EDGE,"E12.1.2"),sQuery(id+"F0.wireOp",EDGE,"E12.1.3"),sQuery(id+"F0.wireOp",EDGE,"E12.1.4"),sQuery(id+"F0.wireOp",EDGE,"E12.1.5"),sQuery(id+"F0.wireOp",EDGE,"E12.2.0"),sQuery(id+"F0.wireOp",EDGE,"E12.2.1"),sQuery(id+"F0.wireOp",EDGE,"E12.2.2"),sQuery(id+"F0.wireOp",EDGE,"E12.2.3"),sQuery(id+"F0.wireOp",EDGE,"E12.2.4"),sQuery(id+"F0.wireOp",EDGE,"E12.2.5"),sQuery(id+"F0.wireOp",EDGE,"E12.3.0"),sQuery(id+"F0.wireOp",EDGE,"E12.3.1"),sQuery(id+"F0.wireOp",EDGE,"E12.3.2"),sQuery(id+"F0.wireOp",EDGE,"E12.3.3"),sQuery(id+"F0.wireOp",EDGE,"E12.3.4"),sQuery(id+"F0.wireOp",EDGE,"E12.3.5"),sQuery(id+"F0.wireOp",EDGE,"E12.4.0"),sQuery(id+"F0.wireOp",EDGE,"E12.4.1"),sQuery(id+"F0.wireOp",EDGE,"E12.4.2"),sQuery(id+"F0.wireOp",EDGE,"E12.4.3"),sQuery(id+"F0.wireOp",EDGE,"E12.4.4"),sQuery(id+"F0.wireOp",EDGE,"E12.4.5"),sQuery(id+"F0.wireOp",EDGE,"E12.5.0"),sQuery(id+"F0.wireOp",EDGE,"E12.5.1"),sQuery(id+"F0.wireOp",EDGE,"E12.5.2"),sQuery(id+"F0.wireOp",EDGE,"E12.5.3"),sQuery(id+"F0.wireOp",EDGE,"E12.5.4"),sQuery(id+"F0.wireOp",EDGE,"E12.5.5"),sQuery(id+"F0.wireOp",EDGE,"E12.6.0"),sQuery(id+"F0.wireOp",EDGE,"E12.6.1"),sQuery(id+"F0.wireOp",EDGE,"E12.6.2"),sQuery(id+"F0.wireOp",EDGE,"E12.6.3"),sQuery(id+"F0.wireOp",EDGE,"E12.6.4"),sQuery(id+"F0.wireOp",EDGE,"E12.6.5"),sQuery(id+"F0.wireOp",EDGE,"E12.7.0"),sQuery(id+"F0.wireOp",EDGE,"E12.7.1"),sQuery(id+"F0.wireOp",EDGE,"E12.7.2"),sQuery(id+"F0.wireOp",EDGE,"E12.7.3"),sQuery(id+"F0.wireOp",EDGE,"E12.7.4"),sQuery(id+"F0.wireOp",EDGE,"E12.7.5"),sQuery(id+"F0.wireOp",EDGE,"E12.8.0"),sQuery(id+"F0.wireOp",EDGE,"E12.8.1"),sQuery(id+"F0.wireOp",EDGE,"E12.8.2"),sQuery(id+"F0.wireOp",EDGE,"E12.8.3"),sQuery(id+"F0.wireOp",EDGE,"E12.8.4"),sQuery(id+"F0.wireOp",EDGE,"E12.8.5"),sQuery(id+"F0.wireOp",EDGE,"E12.9.0"),sQuery(id+"F0.wireOp",EDGE,"E12.9.1"),sQuery(id+"F0.wireOp",EDGE,"E12.9.2"),sQuery(id+"F0.wireOp",EDGE,"E12.9.3"),sQuery(id+"F0.wireOp",EDGE,"E12.9.4"),sQuery(id+"F0.wireOp",EDGE,"E12.9.5"),sQuery(id+"F0.wireOp",EDGE,"E12.10.0"),sQuery(id+"F0.wireOp",EDGE,"E12.10.1"),sQuery(id+"F0.wireOp",EDGE,"E12.10.2"),sQuery(id+"F0.wireOp",EDGE,"E12.10.3"),sQuery(id+"F0.wireOp",EDGE,"E12.10.4"),sQuery(id+"F0.wireOp",EDGE,"E12.10.5"),sQuery(id+"F0.wireOp",EDGE,"E12.11.0"),sQuery(id+"F0.wireOp",EDGE,"E12.11.1"),sQuery(id+"F0.wireOp",EDGE,"E12.11.2"),sQuery(id+"F0.wireOp",EDGE,"E12.11.3"),sQuery(id+"F0.wireOp",EDGE,"E12.11.4"),sQuery(id+"F0.wireOp",EDGE,"E12.11.5"),sQuery(id+"F0.wireOp",EDGE,"E12.12.0"),sQuery(id+"F0.wireOp",EDGE,"E12.12.1"),sQuery(id+"F0.wireOp",EDGE,"E12.12.2"),sQuery(id+"F0.wireOp",EDGE,"E12.12.3"),sQuery(id+"F0.wireOp",EDGE,"E12.12.4"),sQuery(id+"F0.wireOp",EDGE,"E12.12.5"),sQuery(id+"F0.wireOp",EDGE,"E12.13.0"),sQuery(id+"F0.wireOp",EDGE,"E12.13.1"),sQuery(id+"F0.wireOp",EDGE,"E12.13.2"),sQuery(id+"F0.wireOp",EDGE,"E12.13.3"),sQuery(id+"F0.wireOp",EDGE,"E12.13.4"),sQuery(id+"F0.wireOp",EDGE,"E12.13.5"),sQuery(id+"F0.wireOp",EDGE,"E12.14.0"),sQuery(id+"F0.wireOp",EDGE,"E12.14.1"),sQuery(id+"F0.wireOp",EDGE,"E12.14.2"),sQuery(id+"F0.wireOp",EDGE,"E12.14.3"),sQuery(id+"F0.wireOp",EDGE,"E12.14.4"),sQuery(id+"F0.wireOp",EDGE,"E12.14.5"),sQuery(id+"F0.wireOp",EDGE,"E12.15.0"),sQuery(id+"F0.wireOp",EDGE,"E12.15.1"),sQuery(id+"F0.wireOp",EDGE,"E12.15.2"),sQuery(id+"F0.wireOp",EDGE,"E12.15.3"),sQuery(id+"F0.wireOp",EDGE,"E12.15.4"),sQuery(id+"F0.wireOp",EDGE,"E12.15.5"),sQuery(id+"F0.wireOp",EDGE,"E12.16.0"),sQuery(id+"F0.wireOp",EDGE,"E12.16.1"),sQuery(id+"F0.wireOp",EDGE,"E12.16.2"),sQuery(id+"F0.wireOp",EDGE,"E12.16.3"),sQuery(id+"F0.wireOp",EDGE,"E12.16.4"),sQuery(id+"F0.wireOp",EDGE,"E12.16.5"),sQuery(id+"F0.wireOp",EDGE,"E12.17.0"),sQuery(id+"F0.wireOp",EDGE,"E12.17.1"),sQuery(id+"F0.wireOp",EDGE,"E12.17.2"),sQuery(id+"F0.wireOp",EDGE,"E12.17.3"),sQuery(id+"F0.wireOp",EDGE,"E12.17.4"),sQuery(id+"F0.wireOp",EDGE,"E12.17.5"),sQuery(id+"F0.wireOp",EDGE,"E12.18.0"),sQuery(id+"F0.wireOp",EDGE,"E12.18.1"),sQuery(id+"F0.wireOp",EDGE,"E12.18.2"),sQuery(id+"F0.wireOp",EDGE,"E12.18.3"),sQuery(id+"F0.wireOp",EDGE,"E12.18.4"),sQuery(id+"F0.wireOp",EDGE,"E12.18.5"),sQuery(id+"F0.wireOp",EDGE,"E12.19.0"),sQuery(id+"F0.wireOp",EDGE,"E12.19.1"),sQuery(id+"F0.wireOp",EDGE,"E12.19.2"),sQuery(id+"F0.wireOp",EDGE,"E12.19.3"),sQuery(id+"F0.wireOp",EDGE,"E12.19.4"),sQuery(id+"F0.wireOp",EDGE,"E12.19.5"),sQuery(id+"F0.wireOp",EDGE,"E12.20.0"),sQuery(id+"F0.wireOp",EDGE,"E12.20.1"),sQuery(id+"F0.wireOp",EDGE,"E12.20.2"),sQuery(id+"F0.wireOp",EDGE,"E12.20.3"),sQuery(id+"F0.wireOp",EDGE,"E12.20.4"),sQuery(id+"F0.wireOp",EDGE,"E12.20.5"),sQuery(id+"F0.wireOp",EDGE,"E12.21.0"),sQuery(id+"F0.wireOp",EDGE,"E12.21.1"),sQuery(id+"F0.wireOp",EDGE,"E12.21.2"),sQuery(id+"F0.wireOp",EDGE,"E12.21.3"),sQuery(id+"F0.wireOp",EDGE,"E12.21.4"),sQuery(id+"F0.wireOp",EDGE,"E12.21.5"),sQuery(id+"F0.wireOp",EDGE,"E12.22.0"),sQuery(id+"F0.wireOp",EDGE,"E12.22.1"),sQuery(id+"F0.wireOp",EDGE,"E12.22.2"),sQuery(id+"F0.wireOp",EDGE,"E12.22.3"),sQuery(id+"F0.wireOp",EDGE,"E12.22.4"),sQuery(id+"F0.wireOp",EDGE,"E12.22.5"),sQuery(id+"F0.wireOp",EDGE,"E12.23.0"),sQuery(id+"F0.wireOp",EDGE,"E12.23.1"),sQuery(id+"F0.wireOp",EDGE,"E12.23.2"),sQuery(id+"F0.wireOp",EDGE,"E12.23.3"),sQuery(id+"F0.wireOp",EDGE,"E12.23.4"),sQuery(id+"F0.wireOp",EDGE,"E12.23.5"),sQuery(id+"F0.wireOp",EDGE,"E12.24.0"),sQuery(id+"F0.wireOp",EDGE,"E12.24.1"),sQuery(id+"F0.wireOp",EDGE,"E12.24.2"),sQuery(id+"F0.wireOp",EDGE,"E12.24.3"),sQuery(id+"F0.wireOp",EDGE,"E12.24.4"),sQuery(id+"F0.wireOp",EDGE,"E12.24.5"),sQuery(id+"F0.wireOp",EDGE,"E12.25.0"),sQuery(id+"F0.wireOp",EDGE,"E12.25.1"),sQuery(id+"F0.wireOp",EDGE,"E12.25.2"),sQuery(id+"F0.wireOp",EDGE,"E12.25.3"),sQuery(id+"F0.wireOp",EDGE,"E12.25.4"),sQuery(id+"F0.wireOp",EDGE,"E12.25.5"),sQuery(id+"F0.wireOp",EDGE,"E12.26.0"),sQuery(id+"F0.wireOp",EDGE,"E12.26.1"),sQuery(id+"F0.wireOp",EDGE,"E12.26.2"),sQuery(id+"F0.wireOp",EDGE,"E12.26.3"),sQuery(id+"F0.wireOp",EDGE,"E12.26.4"),sQuery(id+"F0.wireOp",EDGE,"E12.26.5"),sQuery(id+"F0.wireOp",EDGE,"E12.27.0"),sQuery(id+"F0.wireOp",EDGE,"E12.27.1"),sQuery(id+"F0.wireOp",EDGE,"E12.27.2"),sQuery(id+"F0.wireOp",EDGE,"E12.27.3"),sQuery(id+"F0.wireOp",EDGE,"E12.27.4"),sQuery(id+"F0.wireOp",EDGE,"E12.27.5"),sQuery(id+"F0.wireOp",EDGE,"E12.28.0"),sQuery(id+"F0.wireOp",EDGE,"E12.28.1"),sQuery(id+"F0.wireOp",EDGE,"E12.28.2"),sQuery(id+"F0.wireOp",EDGE,"E12.28.3"),sQuery(id+"F0.wireOp",EDGE,"E12.28.4"),sQuery(id+"F0.wireOp",EDGE,"E12.28.5"),sQuery(id+"F0.wireOp",EDGE,"E12.29.0"),sQuery(id+"F0.wireOp",EDGE,"E12.29.1"),sQuery(id+"F0.wireOp",EDGE,"E12.29.2"),sQuery(id+"F0.wireOp",EDGE,"E12.29.3"),sQuery(id+"F0.wireOp",EDGE,"E12.29.4"),sQuery(id+"F0.wireOp",EDGE,"E12.29.5"),sQuery(id+"F0.wireOp",EDGE,"E12.30.0"),sQuery(id+"F0.wireOp",EDGE,"E12.30.1"),sQuery(id+"F0.wireOp",EDGE,"E12.30.2"),sQuery(id+"F0.wireOp",EDGE,"E12.30.3"),sQuery(id+"F0.wireOp",EDGE,"E12.30.4"),sQuery(id+"F0.wireOp",EDGE,"E12.30.5"),sQuery(id+"F0.wireOp",EDGE,"E12.31.0"),sQuery(id+"F0.wireOp",EDGE,"E12.31.1"),sQuery(id+"F0.wireOp",EDGE,"E12.31.2"),sQuery(id+"F0.wireOp",EDGE,"E12.31.3"),sQuery(id+"F0.wireOp",EDGE,"E12.31.4"),sQuery(id+"F0.wireOp",EDGE,"E12.31.5"),sQuery(id+"F0.wireOp",EDGE,"E12.32.0"),sQuery(id+"F0.wireOp",EDGE,"E12.32.1"),sQuery(id+"F0.wireOp",EDGE,"E12.32.2"),sQuery(id+"F0.wireOp",EDGE,"E12.32.3"),sQuery(id+"F0.wireOp",EDGE,"E12.32.4"),sQuery(id+"F0.wireOp",EDGE,"E12.32.5"),sQuery(id+"F0.wireOp",EDGE,"E12.33.0"),sQuery(id+"F0.wireOp",EDGE,"E12.33.1"),sQuery(id+"F0.wireOp",EDGE,"E12.33.2"),sQuery(id+"F0.wireOp",EDGE,"E12.33.3"),sQuery(id+"F0.wireOp",EDGE,"E12.33.4"),sQuery(id+"F0.wireOp",EDGE,"E12.33.5"),sQuery(id+"F0.wireOp",EDGE,"E12.34.0"),sQuery(id+"F0.wireOp",EDGE,"E12.34.1"),sQuery(id+"F0.wireOp",EDGE,"E12.34.2"),sQuery(id+"F0.wireOp",EDGE,"E12.34.3"),sQuery(id+"F0.wireOp",EDGE,"E12.34.4"),sQuery(id+"F0.wireOp",EDGE,"E12.34.5"),sQuery(id+"F0.wireOp",EDGE,"E12.35.0"),sQuery(id+"F0.wireOp",EDGE,"E12.35.1"),sQuery(id+"F0.wireOp",EDGE,"E12.35.2"),sQuery(id+"F0.wireOp",EDGE,"E12.35.3"),sQuery(id+"F0.wireOp",EDGE,"E12.35.4"),sQuery(id+"F0.wireOp",EDGE,"E12.35.5"),sQuery(id+"F0.wireOp",EDGE,"E13.trimOffspring"),sQuery(id+"F0.wireOp",EDGE,"E14.trimOffspring"),sQuery(id+"F0.wireOp",EDGE,"E15.trimOffspring"),sQuery(id+"F0.wireOp",EDGE,"E16.trimOffspring"),sQuery(id+"F0.wireOp",EDGE,"E17.trimOffspring"),sQuery(id+"F0.wireOp",EDGE,"E18.trimOffspring"),sQuery(id+"F0.wireOp",EDGE,"E19.trimOffspring"),sQuery(id+"F0.wireOp",EDGE,"E20.trimOffspring"),sQuery(id+"F0.wireOp",EDGE,"E21.trimOffspring"),sQuery(id+"F0.wireOp",EDGE,"E22.trimOffspring"),sQuery(id+"F0.wireOp",EDGE,"E23.trimOffspring"),sQuery(id+"F0.wireOp",EDGE,"E24.trimOffspring"),sQuery(id+"F0.wireOp",EDGE,"E25.trimOffspring"),sQuery(id+"F0.wireOp",EDGE,"E26.trimOffspring"),sQuery(id+"F0.wireOp",EDGE,"E27.trimOffspring"),sQuery(id+"F0.wireOp",EDGE,"E28.trimOffspring"),sQuery(id+"F0.wireOp",EDGE,"E29.trimOffspring"),sQuery(id+"F0.wireOp",EDGE,"E30.trimOffspring"),sQuery(id+"F0.wireOp",EDGE,"E31.trimOffspring"),sQuery(id+"F0.wireOp",EDGE,"E32.trimOffspring"),sQuery(id+"F0.wireOp",EDGE,"E33.trimOffspring"),sQuery(id+"F0.wireOp",EDGE,"E34.trimOffspring"),sQuery(id+"F0.wireOp",EDGE,"E35.trimOffspring"),sQuery(id+"F0.wireOp",EDGE,"E36.trimOffspring"),sQuery(id+"F0.wireOp",EDGE,"E37.trimOffspring"),sQuery(id+"F0.wireOp",EDGE,"E38.trimOffspring"),sQuery(id+"F0.wireOp",EDGE,"E39.trimOffspring"),sQuery(id+"F0.wireOp",EDGE,"E40.trimOffspring"),sQuery(id+"F0.wireOp",EDGE,"E41.trimOffspring"),sQuery(id+"F0.wireOp",EDGE,"E42.trimOffspring"),sQuery(id+"F0.wireOp",EDGE,"E43.trimOffspring"),sQuery(id+"F0.wireOp",EDGE,"E44.trimOffspring"),sQuery(id+"F0.wireOp",EDGE,"E45.trimOffspring"),sQuery(id+"F0.wireOp",EDGE,"E46.trimOffspring"),sQuery(id+"F0.wireOp",EDGE,"E47.trimOffspring")])],"isStart":false});
            var sketch = newSketch(context, id + "F2", { "sketchPlane" : qUnion([Q0])});
            skCircle(sketch, "E48", {"center": v(0, 0) * mm, "radius": 11.43 * mm});
            skSolve(sketch);
        }
        {
            var Q0;
            Q0 = qSketchRegion(id + "F2", true);
            extrude(context, id + "F3", {"entities" : qUnion([Q0]), "operationType" : NewBodyOperationType.ADD, "depth" : 7.37 * mm});
        }
        {
            var Q0;
            Q0=makeQuery(id+"F3.opExtrude","CAP_FACE",FACE,{"disambiguationData":[OSD([sQuery(id+"F2.wireOp",EDGE,"E48")])],"isStart":false});
            var sketch = newSketch(context, id + "F4", { "sketchPlane" : qUnion([Q0])});
            skCircle(sketch, "E49", {"center": v(0, 0) * mm, "radius": 5.59 * mm});
            skCircle(sketch, "E50.cCircle", {"center": v(0, 0) * mm, "radius": 5.59 * mm, "construction": true});
            skLineSegment(sketch, "E50.0", {"start": v(3.23, -5.59) * mm, "end": v(-3.23, -5.59) * mm});
            skLineSegment(sketch, "E50.1", {"start": v(-3.23, -5.59) * mm, "end": v(-6.45, 0) * mm});
            skLineSegment(sketch, "E50.2", {"start": v(-6.45, 0) * mm, "end": v(-3.23, 5.59) * mm});
            skLineSegment(sketch, "E50.3", {"start": v(-3.23, 5.59) * mm, "end": v(3.23, 5.59) * mm});
            skLineSegment(sketch, "E50.4", {"start": v(3.23, 5.59) * mm, "end": v(6.45, 0) * mm});
            skLineSegment(sketch, "E50.5", {"start": v(6.45, 0) * mm, "end": v(3.23, -5.59) * mm});
            skPoint(sketch, "E50.0.midPoint", {"position": v(0, -5.59) * mm});
            skSolve(sketch);
        }
        {
            var Q0;
            Q0 = qSketchRegion(id + "F4", true);
            extrude(context, id + "F5", {"entities" : qUnion([Q0]), "operationType" : NewBodyOperationType.REMOVE, "oppositeDirection" : true, "depth" : 42.67 * mm});
        }
    });
